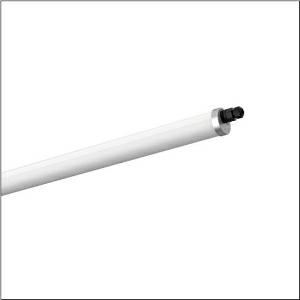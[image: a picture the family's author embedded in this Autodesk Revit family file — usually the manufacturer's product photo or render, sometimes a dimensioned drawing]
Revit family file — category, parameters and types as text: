
# Revit family: monsun_r__31_tube_51ft10dn4a0a_ff33
name_source: partatom
category: Lighting Fixtures
units: mm (PartAtom-declared; Revit-internal decimal feet)

## family parameters
Cut with Voids When Loaded = No
Host = Face
Light Source = No
Part Type = Normal
Room Calculation Point = No
Round Connector Dimension = Use Diameter
Shared = No

## types (1)
- Monsun® 31 Tube (1 x LED, 10000 lm, 58 W, 4000K)
    Apparent Load = 58 VA
    CIE Flux Codes = 42 71 90 91 100
    Color Rendering = 80
    Color Temperature = 4000K
    Default Elevation = 1800 mm
    Description = Monsun® 31 Tube, tubular luminaire, primary optical cover: diffuser, of PMMA, light emission: direct distribution, primary light characteristic: symmetric, installation type: suspended mounting, surface-mounted, LED, rated luminous flux: 10.000lm, luminous efficacy: 160lm/W, light colour: 840, colour temperature: 4000K, control gear: DALI 2, with with 1 terminal, 5-pole, max. 2.5mm², through-wiring: 5x 1.5mm², mains connection: 220..240V, AC, 50/60Hz, rated input power: 58W, housing, cylindrical, of PMMA, semi-transparent, matt white, with luminaire and ceiling fastening, V4A, mounting with brackets of stainless steel, length: 1.570mm, diameter: 75mm, end cap, of stainless steel (V4A), protection rating (complete): IP67/IP69K, insulation class (complete): insulation class I (protective earthing), certification: CE, UKCA, impact resistance: IK07, permissible operating ambient temperature: -20..+40°C, corresponds to IFS (International Featured Standards) requirements for safety and quality in the food industry, usage in unprotected outdoor areas possible with horizontal mounting, contact your sales advisor before using the luminaires in applications with unclear chemical exposure, large temperature fluctuations or condensation-forming humidity, packaging unit: 1 piece
    Height = 83 mm
    Lamp = 1 x LED
    Lamp Light Flux = 10000 lm
    Lamp Power = 58 W
    Lamp count = 1
    Length = 1570 mm
    Luminous efficacy = 172 lm/W
    Manufacturer = Siteco
    ModVariant = No
    Model = 51FT10DN4A0A
    Mounting Place = Ceiling
    Mounting Type = Pendant
    Number of Poles = 1
    OnlyDefault = Yes
    Power Factor = 1
    Product Name = Monsun® 31 Tube
    Product group = tubular luminaire
    ProductGroupID = 907
    Protection Class = Protection class I
    RLX_Detail_Level = 1
    RLX_Emergency_Light_Flux = 0 lm
    RLX_Emergency_Type = 0
    RLX_Emergency_Type_DB = No
    RlxData = <blob elided: 25441 chars, md5=f5ed9b6a>
    Socket = socket
    Standby Power = 0 W
    System Light Flux = 10000 lm
    System Power = 58 W
    Type Comments = Product without accessories
    Type Image = l_1228461.jpg
    URL = http://relux.com
    VarID = ---
    Voltage = 0 V
    Weight = 0.00 kg
    Width = 75 mm

## geometry (parser evidence)
native form markers: Blend x4, Sweep x13
no freeform markers — native parametric forms only
